# Revit family: sh-al5029
name_source: partatom
category: Lighting Fixtures
revit_build: Autodesk Revit 2017 (Build: 20160225_1515(x64)
units: mm (PartAtom-declared; Revit-internal decimal feet)

## family parameters
Always vertical = Yes
Cut with Voids When Loaded = No
Host = Ceiling
Light Source = Yes
OmniClass Number = 23.80.70.11
OmniClass Title = Luminaries for Internal Lighting
Part Type = Normal
Room Calculation Point = No
Round Connector Dimension = Use Diameter
Shared = No

## types (2) — shared parameters
Body Material = Aluminium
Body color = white body
Color Filter = 16777215
Cutting Diameter = 15.5 cm
Default Elevation = 0.0 cm
Diameter = 17.5 cm
Dimming Lamp Color Temperature Shift = <None>
Emit Shape Visible in Rendering = No
Emit from Circle Diameter = 5.0 cm
Flicker = Free Flicker
Height = 10.0 cm
IP = IP20
Lamp = LED
Manufacturer = SHOA
Model = SH-AL5029
Photometric Web File = CFAL5029-30W.ies
Protection Class = class I
Tilt Angle = 90.00°
Type medule = COB
URL = https://www.shoaco.com
Voltage/Frequency = 230V-50HZ
Website = www.shoaco.com
color rendering index(CRI) = 80
color temperature = 4000
consumption current = 0 A
instalation = Recessed
wattage. = 30 W

## type names (no varying parameters)
- SH-AL5029(white Body-4000K-LED)
- SH-AL5029(white Body-3000K-LED)

## geometry (parser evidence)
native form markers: Sweep x1
no freeform markers — native parametric forms only
